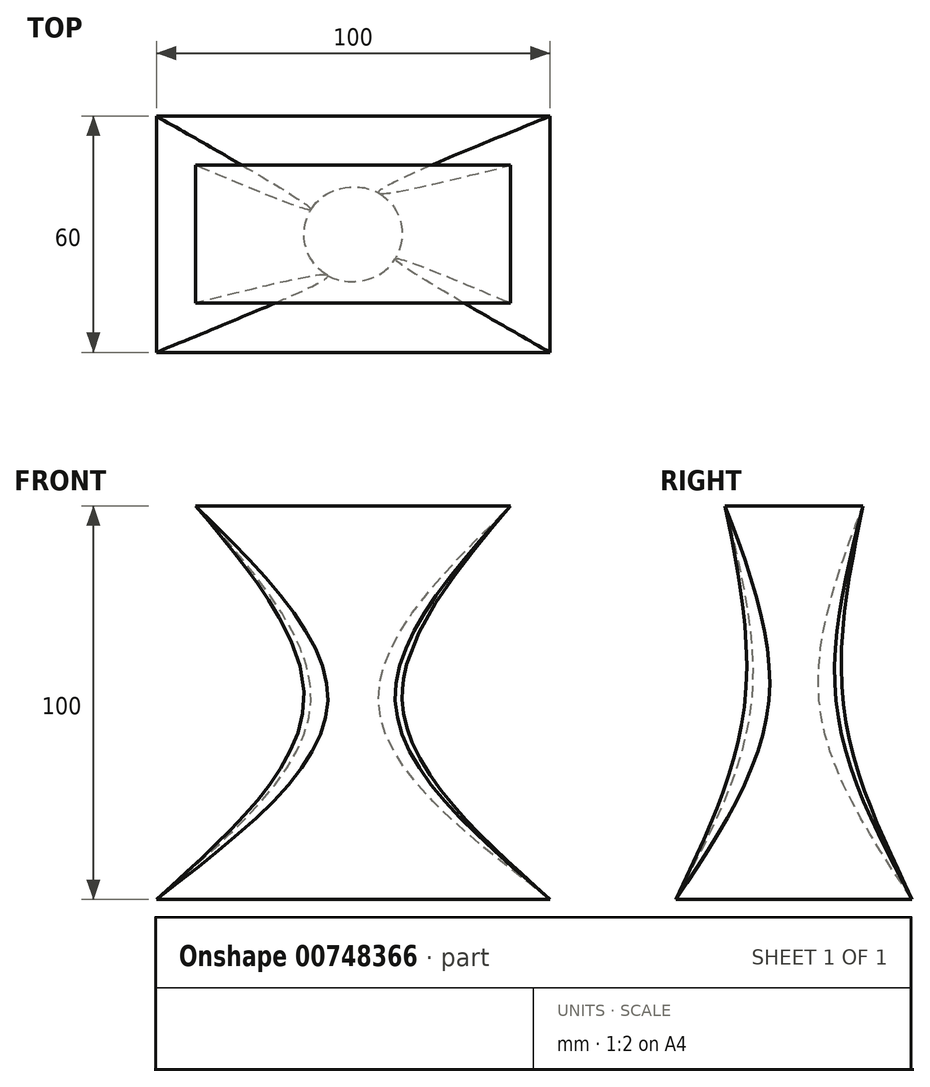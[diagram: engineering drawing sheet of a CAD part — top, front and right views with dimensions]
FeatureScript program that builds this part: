
annotation { "Feature Type Name" : "Feature", "Feature Type Description" : "" }
export const myFeature = defineFeature(function(context is Context, id is Id, definition is map)
    precondition{}
    {
        {
            var Q0;
            Q0=qCreatedBy(makeId("Top.planeOp"),FACE);
            var sketch = newSketch(context, id + "F0", { "sketchPlane" : qUnion([Q0])});
            skLineSegment(sketch, "E0.bottom", {"start": v(50, -30) * mm, "end": v(-50, -30) * mm});
            skLineSegment(sketch, "E0.top", {"start": v(50, 30) * mm, "end": v(-50, 30) * mm});
            skLineSegment(sketch, "E0.left", {"start": v(50, -30) * mm, "end": v(50, 30) * mm});
            skLineSegment(sketch, "E0.right", {"start": v(-50, -30) * mm, "end": v(-50, 30) * mm});
            skPoint(sketch, "E0.middle", {"position": v(0, 0) * mm});
            skSolve(sketch);
        }
        {
            var Q0;
            Q0=qCreatedBy(makeId("Top.planeOp"),FACE);
            cPlane(context, id + "F1", {"entities" : qUnion([Q0]), "cplaneType" : CPlaneType.OFFSET, "offset" : 100 * mm, "width" : 150 * mm, "height" : 150 * mm});
        }
        {
            var Q0;
            Q0=qCreatedBy(id+"F1.planeOp",FACE);
            var sketch = newSketch(context, id + "F2", { "sketchPlane" : qUnion([Q0])});
            skLineSegment(sketch, "E1.bottom", {"start": v(40, 17.5) * mm, "end": v(-40, 17.5) * mm});
            skLineSegment(sketch, "E1.top", {"start": v(40, -17.5) * mm, "end": v(-40, -17.5) * mm});
            skLineSegment(sketch, "E1.left", {"start": v(40, 17.5) * mm, "end": v(40, -17.5) * mm});
            skLineSegment(sketch, "E1.right", {"start": v(-40, 17.5) * mm, "end": v(-40, -17.5) * mm});
            skPoint(sketch, "E1.middle", {"position": v(0, 0) * mm});
            skSolve(sketch);
        }
        {
            var Q0;
            Q0=qCreatedBy(makeId("Top.planeOp"),FACE);
            cPlane(context, id + "F3", {"entities" : qUnion([Q0]), "cplaneType" : CPlaneType.OFFSET, "offset" : 50 * mm, "width" : 150 * mm, "height" : 150 * mm});
        }
        {
            var Q0;
            Q0=qCreatedBy(id+"F3.planeOp",FACE);
            var sketch = newSketch(context, id + "F4", { "sketchPlane" : qUnion([Q0])});
            skCircle(sketch, "E2", {"center": v(0, 0) * mm, "radius": 12.5 * mm});
            skSolve(sketch);
        }
        {
            var Q0;
            Q0=makeQuery(id+"F0.imprint","IMPRINT",FACE,{"disambiguationData":[TD([[makeQuery(id+"F0.imprint","IMPRINT",EDGE,{"derivedFrom":sQuery(id+"F0.wireOp",EDGE,"E0.bottom")}),-1.0]])]});
            var Q1;
            Q1=makeQuery(id+"F4.imprint","IMPRINT",FACE,{"disambiguationData":[TD([[makeQuery(id+"F4.imprint","IMPRINT",EDGE,{"derivedFrom":sQuery(id+"F4.wireOp",EDGE,"E2")}),1.0]])]});
            var Q2;
            Q2=makeQuery(id+"F2.imprint","IMPRINT",FACE,{"disambiguationData":[TD([[makeQuery(id+"F2.imprint","IMPRINT",EDGE,{"derivedFrom":sQuery(id+"F2.wireOp",EDGE,"E1.bottom")}),1.0]])]});
            loft(context, id + "F5", {"sheetProfilesArray" : [{ "sheetProfileEntities" : qUnion([Q0]) }, { "sheetProfileEntities" : qUnion([Q1]) }, { "sheetProfileEntities" : qUnion([Q2]) }]});
        }
    });
